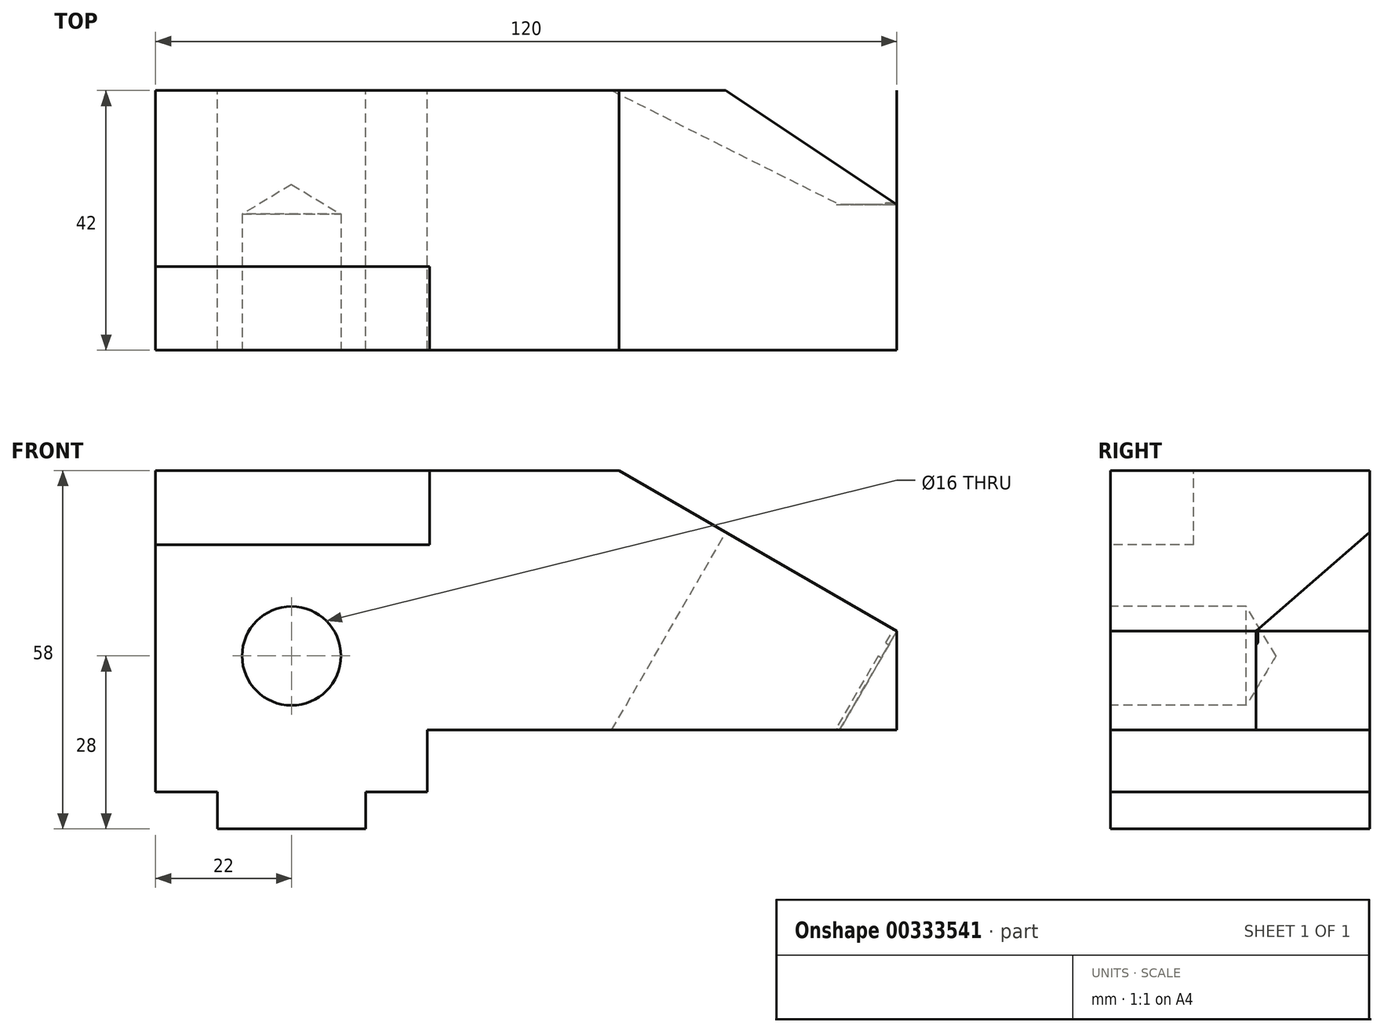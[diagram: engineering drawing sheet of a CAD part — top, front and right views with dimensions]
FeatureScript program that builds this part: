
annotation { "Feature Type Name" : "Feature", "Feature Type Description" : "" }
export const myFeature = defineFeature(function(context is Context, id is Id, definition is map)
    precondition{}
    {
        {
            var Q0;
            Q0=qCreatedBy(makeId("Front.planeOp"),FACE);
            var sketch = newSketch(context, id + "F0", { "sketchPlane" : qUnion([Q0])});
            skLineSegment(sketch, "E0.bottom", {"start": v(0, 0) * mm, "end": v(120, 0) * mm});
            skLineSegment(sketch, "E0.top", {"start": v(0, 42) * mm, "end": v(75, 42) * mm});
            skLineSegment(sketch, "E0.left", {"start": v(0, 0) * mm, "end": v(0, 42) * mm});
            skLineSegment(sketch, "E1", {"start": v(75, 42) * mm, "end": v(120, 16.02) * mm});
            skLineSegment(sketch, "E2", {"start": v(120, 16.02) * mm, "end": v(120, 0) * mm});
            skLineSegment(sketch, "E3", {"start": v(120, 0) * mm, "end": v(0, 0) * mm});
            skLineSegment(sketch, "E4", {"start": v(0, 30) * mm, "end": v(44, 30) * mm});
            skLineSegment(sketch, "E5", {"start": v(44, 30) * mm, "end": v(44, -10) * mm});
            skLineSegment(sketch, "E6", {"start": v(44, -10) * mm, "end": v(34, -10) * mm});
            skLineSegment(sketch, "E7", {"start": v(34, -10) * mm, "end": v(34, -16) * mm});
            skLineSegment(sketch, "E8", {"start": v(34, -16) * mm, "end": v(10, -16) * mm});
            skLineSegment(sketch, "E9", {"start": v(10, -16) * mm, "end": v(10, -10) * mm});
            skLineSegment(sketch, "E10", {"start": v(10, -10) * mm, "end": v(0, -10) * mm});
            skLineSegment(sketch, "E11", {"start": v(0, -10) * mm, "end": v(0, 0) * mm});
            skPoint(sketch, "E12", {"position": v(22, 12) * mm});
            skSolve(sketch);
        }
        {
            var Q0;
            Q0 = qSketchRegion(id + "F0", true);
            extrude(context, id + "F1", {"entities" : qUnion([Q0]), "depth" : 42 * mm});
        }
        {
            var Q0;
            Q0=makeQuery(id+"F1.opExtrude","CAP_FACE",FACE,{"disambiguationData":[OSD([sQuery(id+"F0.wireOp",EDGE,"E0.top"),sQuery(id+"F0.wireOp",EDGE,"E0.left"),sQuery(id+"F0.wireOp",EDGE,"E1"),sQuery(id+"F0.wireOp",EDGE,"E2"),sQuery(id+"F0.wireOp",EDGE,"E3"),sQuery(id+"F0.wireOp",EDGE,"E5"),sQuery(id+"F0.wireOp",EDGE,"E6"),sQuery(id+"F0.wireOp",EDGE,"E7"),sQuery(id+"F0.wireOp",EDGE,"E8"),sQuery(id+"F0.wireOp",EDGE,"E9"),sQuery(id+"F0.wireOp",EDGE,"E10"),sQuery(id+"F0.wireOp",EDGE,"E11")])],"isStart":false});
            var sketch = newSketch(context, id + "F2", { "sketchPlane" : qUnion([Q0])});
            skPoint(sketch, "E13", {"position": v(22, 12) * mm});
            skSolve(sketch);
        }
        {
            var Q0;
            Q0=sQuery(id+"F2.wireOp",VERTEX,"E13");
            var Q1;
            Q1=makeQuery(id+"F1.opExtrude","SWEPT_BODY",BODY,{"disambiguationData":[OSD([sQuery(id+"F0.wireOp",EDGE,"E0.top"),sQuery(id+"F0.wireOp",EDGE,"E0.left"),sQuery(id+"F0.wireOp",EDGE,"E1"),sQuery(id+"F0.wireOp",EDGE,"E2"),sQuery(id+"F0.wireOp",EDGE,"E3"),sQuery(id+"F0.wireOp",EDGE,"E5"),sQuery(id+"F0.wireOp",EDGE,"E6"),sQuery(id+"F0.wireOp",EDGE,"E7"),sQuery(id+"F0.wireOp",EDGE,"E8"),sQuery(id+"F0.wireOp",EDGE,"E9"),sQuery(id+"F0.wireOp",EDGE,"E10"),sQuery(id+"F0.wireOp",EDGE,"E11")])]});
            hole(context, id + "F3", {"style" : HoleStyle.SIMPLE, "endStyle" : HoleEndStyle.BLIND, "holeDiameter" : 16 * mm, "holeDepth" : 22 * mm, "tappedDepth" : 12 * mm, "tapClearance" : 3, "locations" : qUnion([Q0]), "scope" : qUnion([Q1])});
        }
        {
            var Q0;
            Q0=makeQuery(id+"F1.opExtrude","CAP_FACE",FACE,{"disambiguationData":[OSD([sQuery(id+"F0.wireOp",EDGE,"E0.top"),sQuery(id+"F0.wireOp",EDGE,"E0.left"),sQuery(id+"F0.wireOp",EDGE,"E1"),sQuery(id+"F0.wireOp",EDGE,"E2"),sQuery(id+"F0.wireOp",EDGE,"E3"),sQuery(id+"F0.wireOp",EDGE,"E5"),sQuery(id+"F0.wireOp",EDGE,"E6"),sQuery(id+"F0.wireOp",EDGE,"E7"),sQuery(id+"F0.wireOp",EDGE,"E8"),sQuery(id+"F0.wireOp",EDGE,"E9"),sQuery(id+"F0.wireOp",EDGE,"E10"),sQuery(id+"F0.wireOp",EDGE,"E11")])],"isStart":false});
            var sketch = newSketch(context, id + "F4", { "sketchPlane" : qUnion([Q0])});
            skLineSegment(sketch, "E14", {"start": v(44.38, 30) * mm, "end": v(0, 30) * mm});
            skLineSegment(sketch, "E15", {"start": v(0, 30) * mm, "end": v(0, 42) * mm});
            skLineSegment(sketch, "E16", {"start": v(0, 42) * mm, "end": v(44.38, 42) * mm});
            skLineSegment(sketch, "E17", {"start": v(44.38, 42) * mm, "end": v(44.38, 30) * mm});
            skSolve(sketch);
        }
        {
            var Q0;
            Q0 = qSketchRegion(id + "F4", true);
            extrude(context, id + "F5", {"entities" : qUnion([Q0]), "operationType" : NewBodyOperationType.REMOVE, "oppositeDirection" : true, "depth" : 13.5 * mm});
        }
        {
            var Q0;
            {var subQ2=sQuery(id+"F0.wireOp",EDGE,"E0.top");Q0=makeQuery(id+"F0.imprint","IMPRINT",FACE,{"disambiguationData":[TD([[makeQuery(id+"F0.imprint","IMPRINT",EDGE,{"derivedFrom":subQ2}),-1.0]])]});}
            var sketch = newSketch(context, id + "F6", { "sketchPlane" : qUnion([Q0])});
            skLineSegment(sketch, "E18.bottom", {"start": v(0, 30) * mm, "end": v(44, 30) * mm});
            skLineSegment(sketch, "E18.top", {"start": v(0, 42) * mm, "end": v(44, 42) * mm});
            skLineSegment(sketch, "E18.left", {"start": v(0, 30) * mm, "end": v(0, 42) * mm});
            skLineSegment(sketch, "E18.right", {"start": v(44, 30) * mm, "end": v(44, 42) * mm});
            skSolve(sketch);
        }
        {
            var Q0;
            Q0=makeQuery(id+"F1.opExtrude","SWEPT_FACE",FACE,{"disambiguationData":[OSD([sQuery(id+"F0.wireOp",EDGE,"E1")])]});
            var sketch = newSketch(context, id + "F7", { "sketchPlane" : qUnion([Q0])});
            skLineSegment(sketch, "E19", {"start": v(43.95, 0) * mm, "end": v(63.95, 0) * mm});
            skLineSegment(sketch, "E20", {"start": v(63.95, 0) * mm, "end": v(95.91, -18.45) * mm});
            skLineSegment(sketch, "E21", {"start": v(95.91, -18.45) * mm, "end": v(95.91, -42) * mm});
            skLineSegment(sketch, "E22", {"start": v(95.91, -42) * mm, "end": v(43.95, -42) * mm});
            skLineSegment(sketch, "E23", {"start": v(43.95, -42) * mm, "end": v(43.95, 0) * mm});
            skSolve(sketch);
        }
        {
            var Q0;
            {var subQ0=sQuery(id+"F7.wireOp",EDGE,"E20");Q0=makeQuery(id+"F7.imprint","IMPRINT",FACE,{"disambiguationData":[TD([[makeQuery(id+"F7.imprint","IMPRINT",EDGE,{"derivedFrom":subQ0}),1.0]])]});}
            extrude(context, id + "F8", {"entities" : qUnion([Q0]), "operationType" : NewBodyOperationType.REMOVE, "endBound" : BoundingType.THROUGH_ALL, "oppositeDirection" : true, "depth" : 5 * mm});
        }
        {
            var Q0;
            {var subQ3=sQuery(id+"F6.wireOp",EDGE,"E18.right");Q0=makeQuery(id+"F6.imprint","IMPRINT",FACE,{"disambiguationData":[TD([[makeQuery(id+"F6.imprint","IMPRINT",EDGE,{"derivedFrom":subQ3}),-1.0]])]});}
            var sketch = newSketch(context, id + "F9", { "sketchPlane" : qUnion([Q0])});
            skLineSegment(sketch, "E24", {"start": v(120, 16.01) * mm, "end": v(110.71, 0) * mm});
            skLineSegment(sketch, "E25", {"start": v(110.71, 0) * mm, "end": v(120.14, 0) * mm});
            skLineSegment(sketch, "E26", {"start": v(120.14, 0) * mm, "end": v(120, 16.01) * mm});
            skSolve(sketch);
        }
        {
            var Q0;
            Q0 = qSketchRegion(id + "F9", true);
            extrude(context, id + "F10", {"entities" : qUnion([Q0]), "operationType" : NewBodyOperationType.REMOVE, "depth" : 18.45 * mm});
        }
        {
            var Q0;
            Q0=makeQuery(id+"F10.boolean.opBoolean","COPY",FACE,{"derivedFrom":makeQuery(id+"F10.opExtrude","SWEPT_FACE",FACE,{"disambiguationData":[OSD([sQuery(id+"F9.wireOp",EDGE,"E24")])]})});
            extrude(context, id + "F11", {"entities" : qUnion([Q0]), "operationType" : NewBodyOperationType.REMOVE, "oppositeDirection" : true, "depth" : .6 * mm});
        }
    });
